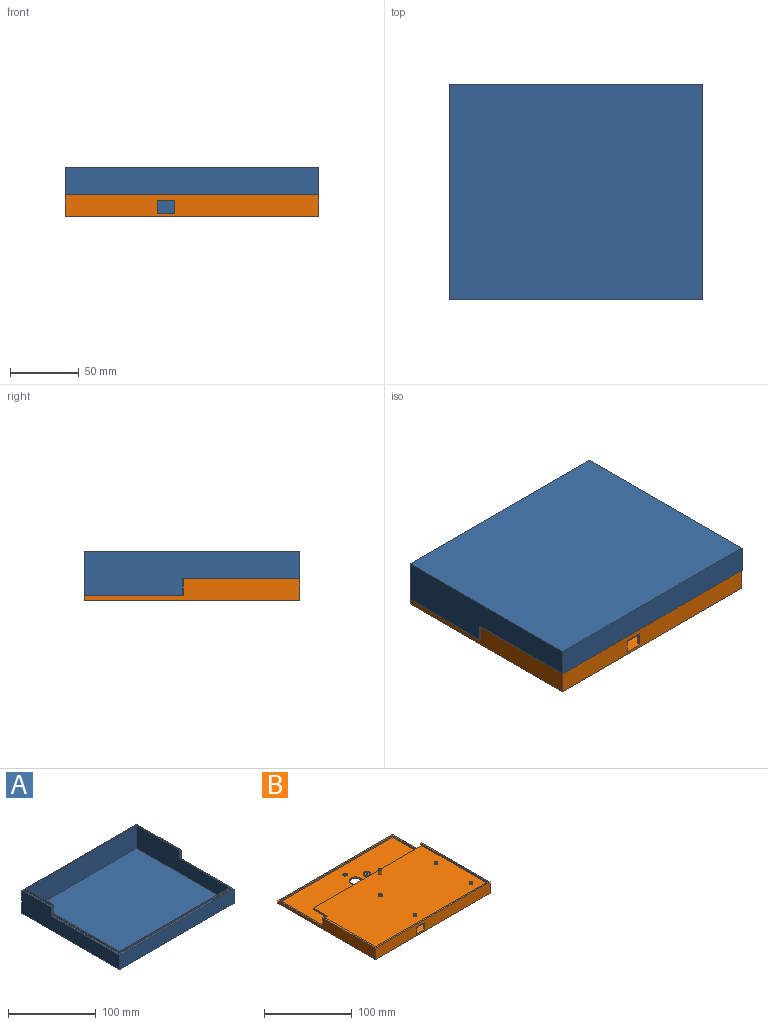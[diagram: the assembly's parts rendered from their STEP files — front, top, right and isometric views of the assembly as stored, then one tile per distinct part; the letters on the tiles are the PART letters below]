
ASSEMBLY  parts=2 mates=1
PART A: 22 faces, bbox 185x157x34 mm
  f0: plane 14x3.5mm, normal (0,-1,0), area 42mm2, adj f1,f3,f7,f13,f14,f17,f20,f21
  f1: plane 185x110mm, normal (0,0,1), area 863.4mm2, adj f0,f3,f4,f5,f12,f14,f15,f16
  f2: plane 185x32mm, normal (0,1,0), area 5920mm2, adj f3,f5,f6,f13
  f3: plane 157x32mm, normal (-1,0,0), area 3704mm2, adj f0,f1,f2,f4,f6,f13
  f4: plane 185x20mm, normal (0,-1,0), area 3700mm2, adj f1,f3,f5,f6
  f5: plane 157x32mm, normal (1,0,0), area 4004mm2, adj f1,f2,f4,f6,f12,f13
  f6: plane 185x157mm, normal (0,0,-1), area 29045mm2, adj f2,f3,f4,f5
  f7: plane 150x32mm, normal (1,0,0), area 3522mm2, adj f0,f8,f10,f11,f17,f21
  f8: plane 178x32mm, normal (0,-1,0), area 5696mm2, adj f7,f9,f11,f21
  f9: plane 150x32mm, normal (-1,0,0), area 3822mm2, adj f8,f10,f11,f12,f17,f21
  f10: plane 178x20mm, normal (0,1,0), area 3560mm2, adj f7,f9,f11,f17
  f11: plane 178x150mm, normal (0,0,1), area 26700mm2, adj f7,f8,f9,f10
  f12: plane 14x3.5mm, normal (0,-1,0), area 42mm2, adj f1,f5,f9,f13,f16,f17,f18,f21
  f13: plane 185x72mm, normal (0,0,1), area 688.6mm2, adj f0,f2,f3,f5,f12,f18,f19,f20
  f14: plane 107.7x2mm, normal (-1,0,0), area 215.4mm2, adj f0,f1,f15,f17
  f15: plane 180.4x2mm, normal (0,-1,0), area 360.8mm2, adj f1,f14,f16,f17
  f16: plane 82.7x2mm, normal (1,0,0), area 165.4mm2, adj f1,f12,f15,f17
  f17: plane 180.4x107.7mm, normal (0,0,1), area 442.1mm2, adj f0,f7,f9,f10,f12,f14,f15,f16
  f18: plane 69.7x2mm, normal (1,0,0), area 139.4mm2, adj f12,f13,f19,f21
  f19: plane 180.4x2mm, normal (0,1,0), area 360.8mm2, adj f13,f18,f20,f21
  f20: plane 44.7x2mm, normal (-1,0,0), area 89.4mm2, adj f0,f13,f19,f21
  f21: plane 180.4x69.7mm, normal (0,0,1), area 350.9mm2, adj f0,f7,f8,f9,f12,f18,f19,f20
PART B: 54 faces, bbox 185x157x20 mm
  f0: plane 180x108mm, normal (0,0,-1), area 18961mm2, adj f14,f17,f18,f19,f20,f21,f24,f27
  f1: cylinder r=3.75mm len=7.5mm, axis (0,0,1), area 23.6mm2, adj f40,f50
  f2: cylinder r=4.5mm len=9mm, axis (0,0,-1), area 28.3mm2, adj f48,f50
  f3: plane 185x4mm, normal (0,1,0), area 740mm2, adj f4,f5,f49,f51
  f4: plane 157x16mm, normal (-1,0,0), area 1648mm2, adj f3,f18,f47,f49,f51,f52
  f5: plane 157x16mm, normal (1,0,0), area 1948mm2, adj f3,f18,f42,f47,f49,f51
  f6: plane 180.87x2mm, normal (0,-1,0), area 361.7mm2, adj f20,f41,f48,f49
  f7: plane 152.72x2mm, normal (0,1,0), area 305.4mm2, adj f9,f10,f48,f51
  f8: plane 152.72x2mm, normal (0,-1,0), area 305.4mm2, adj f9,f10,f48,f51
  f9: plane 89.06x2mm, normal (-1,0,0), area 178.1mm2, adj f7,f8,f48,f51
  f10: plane 89.06x2mm, normal (1,0,0), area 178.1mm2, adj f7,f8,f48,f51
  f11: cylinder r=2.75mm len=5.5mm, axis (0,0,1), area 34.6mm2, adj f48,f51
  f12: cylinder r=7.5mm len=15mm, axis (0,0,1), area 94.2mm2, adj f48,f51
  f13: plane 180.87x106mm, normal (0,0,1), area 18971.1mm2, adj f14,f22,f25,f28,f31,f36,f44,f45
  f14: plane 174.87x2mm, normal (0,1,0), area 349.7mm2, adj f0,f13,f15,f43,f53
  f15: plane 10x0.87mm, normal (0,1,0), area 8.7mm2, adj f14,f38,f41,f48
  f16: cylinder r=1mm len=2mm, axis (0,0,1), area 12.6mm2, adj f40,f51
  f17: plane 102.13x10mm, normal (0,1,0), area 1021.3mm2, adj f0,f34,f38,f48
  f18: plane 185x16mm, normal (0,-1,0), area 2830mm2, adj f0,f4,f5,f33,f34,f47,f48,f51
  f19: plane 64.87x10mm, normal (0,1,0), area 648.7mm2, adj f0,f20,f33,f48
  f20: plane 153x10mm, normal (1,0,0), area 970mm2, adj f0,f6,f19,f48,f49,f52
  f21: cylinder r=0.75mm len=4mm, axis (0,0,-1), area 18.8mm2, adj f0,f23
  f22: cylinder r=2mm len=4mm, axis (0,0,-1), area 25.1mm2, adj f13,f23
  f23: plane 4x4mm, normal (0,0,1), area 10.8mm2, adj f21,f22
  f24: cylinder r=0.75mm len=4mm, axis (0,0,-1), area 18.8mm2, adj f0,f26
  f25: cylinder r=2mm len=4mm, axis (0,0,-1), area 25.1mm2, adj f13,f26
  f26: plane 4x4mm, normal (0,0,1), area 10.8mm2, adj f24,f25
  f27: cylinder r=0.75mm len=4mm, axis (0,0,-1), area 18.8mm2, adj f0,f29
  f28: cylinder r=2mm len=4mm, axis (0,0,-1), area 25.1mm2, adj f13,f29
  f29: plane 4x4mm, normal (0,0,1), area 10.8mm2, adj f27,f28
  f30: cylinder r=0.75mm len=4mm, axis (0,0,-1), area 18.8mm2, adj f0,f32
  f31: cylinder r=2mm len=4mm, axis (0,0,-1), area 25.1mm2, adj f13,f32
  f32: plane 4x4mm, normal (0,0,1), area 10.8mm2, adj f30,f31
  f33: plane 10x2mm, normal (1,0,0), area 20mm2, adj f0,f18,f19,f48
  f34: plane 10x2mm, normal (-1,0,0), area 20mm2, adj f0,f17,f18,f48
  f35: cylinder r=0.75mm len=4mm, axis (0,0,-1), area 18.8mm2, adj f37,f39
  f36: cylinder r=2mm len=6mm, axis (0,0,-1), area 75.4mm2, adj f13,f37
  f37: plane 4x4mm, normal (0,0,1), area 10.8mm2, adj f35,f36
  f38: plane 106x10mm, normal (-1,0,0), area 1060mm2, adj f0,f15,f17,f48
  f39: plane 1.5x1.5mm, normal (0,0,1), area 1.8mm2, adj f35
  f40: plane 7.5x7.5mm, normal (0,0,1), area 41mm2, adj f1,f16
  f41: plane 47x10mm, normal (-1,0,0), area 110mm2, adj f6,f15,f42,f43,f48,f49
  f42: plane 12x2mm, normal (0,1,0), area 24mm2, adj f5,f41,f43,f47,f49
  f43: plane 4x2mm, normal (-1,0,0), area 8mm2, adj f14,f41,f42,f45,f47
  f44: plane 83x2mm, normal (1,0,0), area 166mm2, adj f13,f46,f47,f52
  f45: plane 106x2mm, normal (-1,0,0), area 212mm2, adj f13,f43,f46,f47
  f46: plane 180.87x2mm, normal (0,1,0), area 361.7mm2, adj f13,f44,f45,f47
  f47: plane 185x110mm, normal (0,0,1), area 763.2mm2, adj f4,f5,f18,f42,f43,f44,f45,f46
  f48: plane 180.87x155mm, normal (0,0,1), area 13741.5mm2, adj f2,f6,f7,f8,f9,f10,f11,f12
  f49: plane 185x72mm, normal (0,0,1), area 609.2mm2, adj f3,f4,f5,f6,f20,f41,f42,f52
  f50: plane 9x9mm, normal (0,0,1), area 19.4mm2, adj f1,f2
  f51: plane 185x157mm, normal (0,0,-1), area 15240.1mm2, adj f3,f4,f5,f7,f8,f9,f10,f11
  f52: plane 12x8.13mm, normal (0,1,0), area 37.6mm2, adj f0,f4,f13,f20,f44,f47,f49,f53
  f53: plane 23x2mm, normal (-1,0,0), area 46mm2, adj f0,f13,f14,f52
PLACE A rot(axis=(0,-1,0),180deg) t=(65.56,166.77,59.22)mm
PLACE B rot(axis=(1,0,0),0deg) t=(-1.08,95.22,23.22)mm
MATE parallel B.f49 <-> A.f13  axis (0,0,1) through (10.5,213.74,27.22)mm
